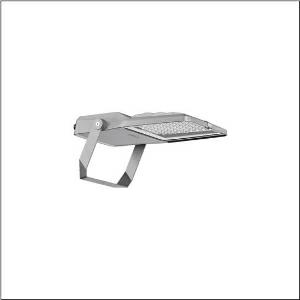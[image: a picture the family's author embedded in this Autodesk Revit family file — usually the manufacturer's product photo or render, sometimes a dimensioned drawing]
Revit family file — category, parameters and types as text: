
# Revit family: floodlight_fl_21_mini___pl52_5xa7776b2d1a_de24
name_source: partatom
category: Lighting Fixtures
units: mm (PartAtom-declared; Revit-internal decimal feet)

## family parameters
Cut with Voids When Loaded = No
Host = Face
Light Source = No
Part Type = Normal
Room Calculation Point = No
Round Connector Dimension = Use Diameter
Shared = No

## types (1)
- --- (1 x LED, 6230 lm, 45.7 W, 3000K)
    Apparent Load = 46 VA
    CIE Flux Codes = 26 60 98 100 100
    Color Rendering = 70
    Color Temperature = 3000K
    Default Elevation = 1800 mm
    Description = Floodlight FL 21 mini, floodlight, primary light control with lens, of PMMA, primary optical cover: protective disc, of toughened safety glass, transparent, light distribution: PL52, light emission: direct distribution, installation type: surface-mounted, LED, High Power LED, rated luminous flux: 6.230lm, luminous efficacy: 136lm/W, light colour: 730, colour temperature: 3000K, control gear: Smart Interface (Zhaga), control: flexible luminous flux parameterisation, time-dependent luminous flux control, constant luminous flux control, overheat protection, pre-setting: logarithmic dimming characteristic, with terminal, 6-pole, mains connection: 220..240V, AC, 50/60Hz, start of lifetime: 46W, end of service life: 48W, reduction: 22W, luminaire housing, of diecast aluminium, powder-coated, SITECO metallic grey (DB 702S), corrosivity category C5 mid according to DIN EN ISO 12944, suitable for swimming pools, chlorine-resistant, sealing non-destructively replaceable, mounting bracket, of steel, galvanised, powder-coated, SITECO metallic grey (DB 702S), Smart Interface below and above, protection rating (complete): IP66, insulation class (complete): insulation class II (safety insulation), certification: CE, ENEC, VDE, protection symbol: D, impact resistance: IK08, permissible operating ambient temperature: -40..+40°C, permissible operating ambient temperature for outdoor applications: -40..+50°C, standard: DIN EN 12944, LABS conformity tested according to VDMA 24364:2018-05, packaging unit: 1 piece

Light Distribution: PL52
    Height = 70 mm
    Lamp = 1 x LED
    Lamp Light Flux = 6230 lm
    Lamp Power = 45.7 W
    Lamp count = 1
    Length = 485 mm
    Luminous efficacy = 136 lm/W
    Manufacturer = Siteco
    ModVariant = No
    Model = 5XA7776B2D1A
    Number of Poles = 1
    OnlyDefault = Yes
    Power Factor = 1
    Product Name = Floodlight FL 21 mini | PL52
    Product group = floodlight | pylon annexe
    ProductGroupID = 6201
    Protection Class = Protection class II
    Protection Degree = IP 66
    RLX_Detail_Level = 1
    RLX_Emergency_Light_Flux = 0 lm
    RLX_Emergency_Type = 0
    RLX_Emergency_Type_DB = No
    RlxData = <blob elided: 96201 chars, md5=c0f31d69>
    Socket = socket
    Standby Power = 0 W
    System Light Flux = 6230 lm
    System Power = 46 W
    Type Comments = factory setting: luminous flux: 100 % | dim-lin: 254 | 463 mA
    Type Image = l_1006845.jpg
    URL = http://relux.com
    VarID = @adj_162889
    Voltage = 0 V
    Weight = 0.00 kg
    Width = 337 mm

## geometry (parser evidence)
native form markers: Blend x4, Sweep x12
no freeform markers — native parametric forms only
